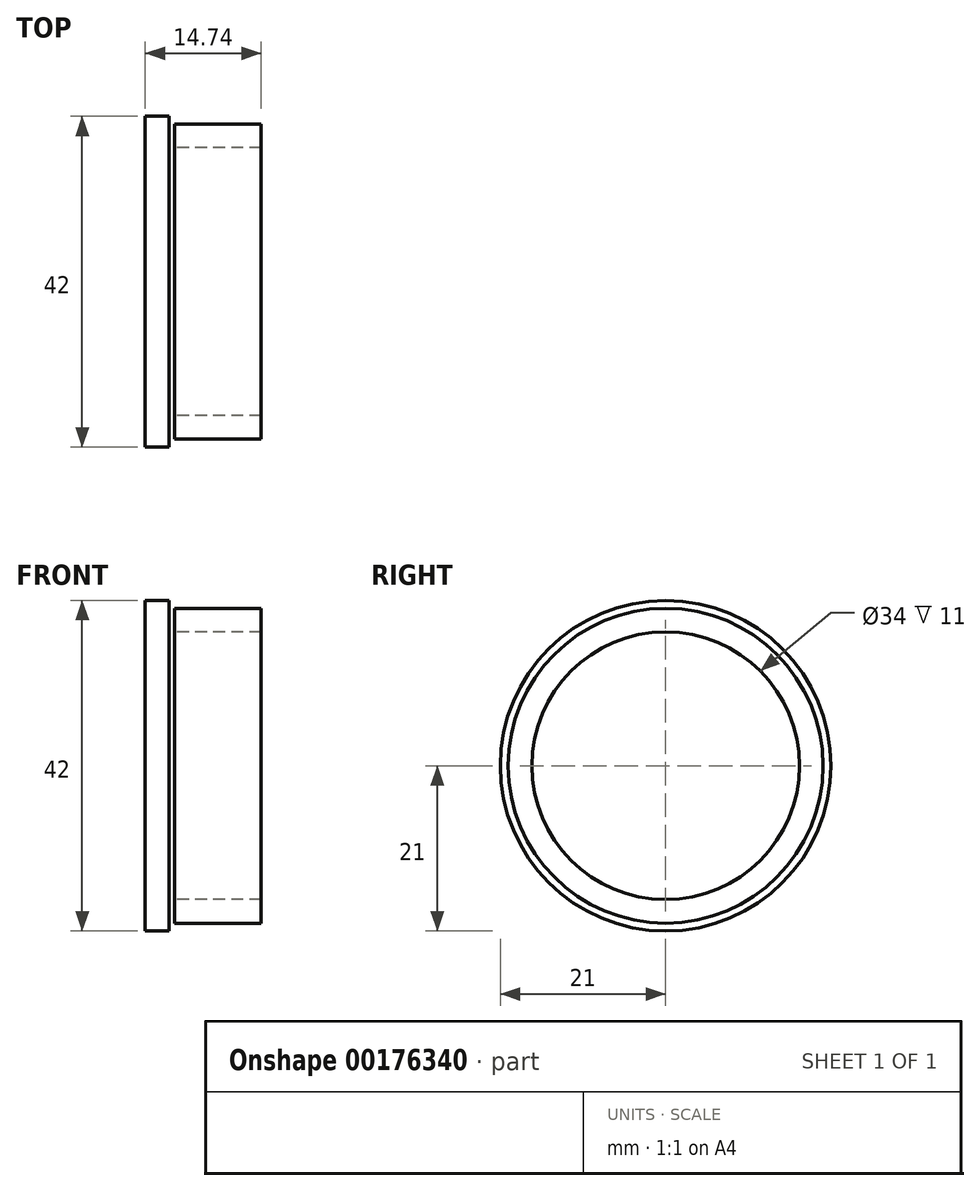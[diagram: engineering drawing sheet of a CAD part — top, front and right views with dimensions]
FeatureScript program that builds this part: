
annotation { "Feature Type Name" : "Feature", "Feature Type Description" : "" }
export const myFeature = defineFeature(function(context is Context, id is Id, definition is map)
    precondition{}
    {
        {
            var Q0;
            Q0=qCreatedBy(makeId("Front.planeOp"),FACE);
            var sketch = newSketch(context, id + "F0", { "sketchPlane" : qUnion([Q0])});
            skLineSegment(sketch, "E0.bottom", {"start": v(0, 0) * mm, "end": v(3, 0) * mm});
            skLineSegment(sketch, "E0.top", {"start": v(0, 21) * mm, "end": v(3, 21) * mm});
            skLineSegment(sketch, "E0.left", {"start": v(0, 0) * mm, "end": v(0, 21) * mm});
            skLineSegment(sketch, "E0.right", {"start": v(3, 0) * mm, "end": v(3, 21) * mm});
            skSolve(sketch);
        }
        {
            var Q0;
            Q0=qSketchRegion(id+"F0",true);
            var Q1;
            Q1=sQuery(id+"F0.wireOp",EDGE,"E0.bottom");
            revolve(context, id + "F1", {"entities" : qUnion([Q0]), "axis" : qUnion([Q1]), "revolveType" : RevolveType.FULL});
        }
        {
            var Q0;
            Q0=qCreatedBy(makeId("Front.planeOp"),FACE);
            var sketch = newSketch(context, id + "F2", { "sketchPlane" : qUnion([Q0])});
            skPoint(sketch, "E1.bottom.start.orphan", {"position": v(2.15, 0) * mm});
            skLineSegment(sketch, "E2.bottom", {"start": v(3.74, 0) * mm, "end": v(14.74, 0) * mm});
            skLineSegment(sketch, "E2.top", {"start": v(3.74, 17) * mm, "end": v(14.74, 17) * mm});
            skLineSegment(sketch, "E2.left", {"start": v(3.74, 0) * mm, "end": v(3.74, 17) * mm});
            skLineSegment(sketch, "E2.right", {"start": v(14.74, 0) * mm, "end": v(14.74, 17) * mm});
            skLineSegment(sketch, "E3.top", {"start": v(3.74, 20) * mm, "end": v(14.74, 20) * mm});
            skLineSegment(sketch, "E3.left", {"start": v(3.74, 0) * mm, "end": v(3.74, 20) * mm});
            skLineSegment(sketch, "E3.right", {"start": v(14.74, 0) * mm, "end": v(14.74, 20) * mm});
            skSolve(sketch);
        }
        {
            var Q0;
            {var subQ0=sQuery(id+"F2.wireOp",EDGE,"E2.top");Q0=makeQuery(id+"F2.imprint","IMPRINT",FACE,{"disambiguationData":[TD([[makeQuery(id+"F2.imprint","IMPRINT",EDGE,{"derivedFrom":subQ0}),1.0]])]});}
            var Q1;
            Q1=sQuery(id+"F2.wireOp",EDGE,"E2.bottom");
            revolve(context, id + "F3", {"entities" : qUnion([Q0]), "axis" : qUnion([Q1]), "revolveType" : RevolveType.FULL});
        }
    });
